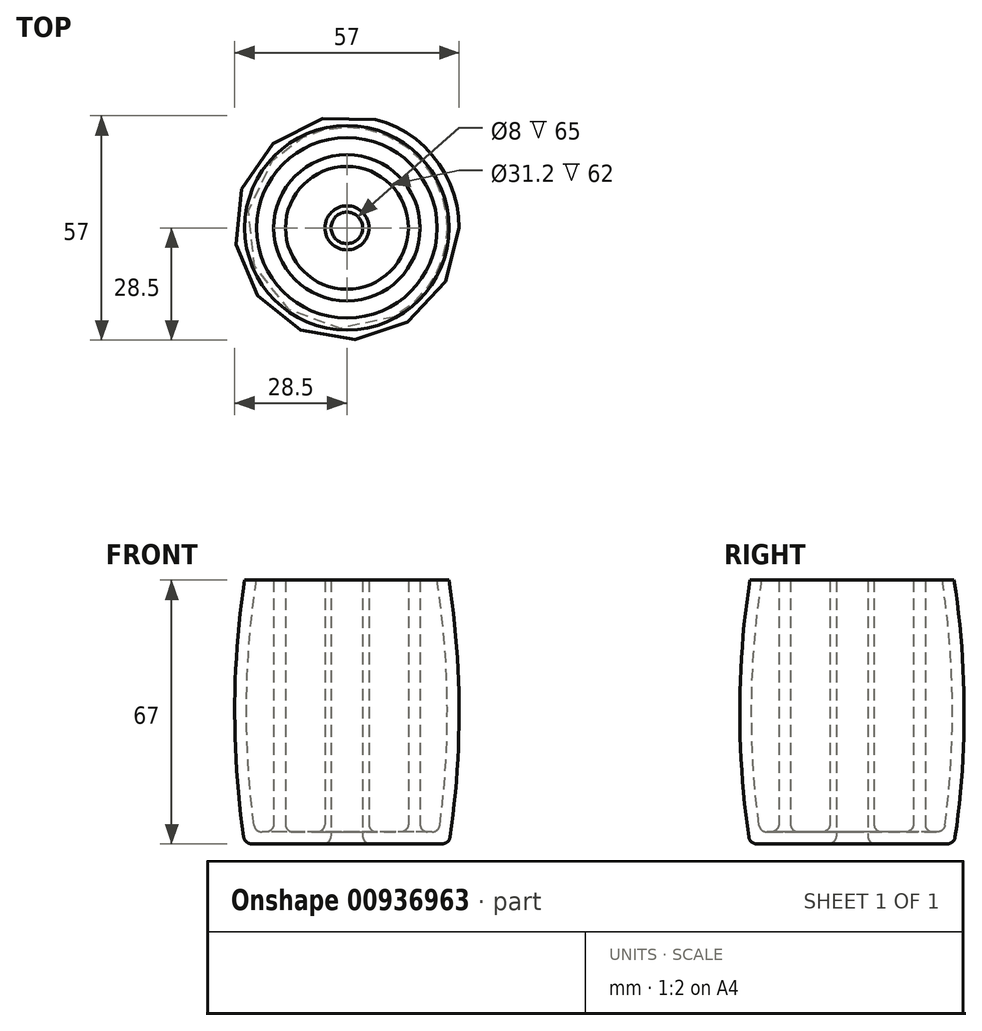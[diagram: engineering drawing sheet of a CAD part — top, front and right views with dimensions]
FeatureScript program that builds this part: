
annotation { "Feature Type Name" : "Feature", "Feature Type Description" : "" }
export const myFeature = defineFeature(function(context is Context, id is Id, definition is map)
    precondition{}
    {
        {
            var Q0;
            Q0=qCreatedBy(makeId("Front.planeOp"),FACE);
            var sketch = newSketch(context, id + "F0", { "sketchPlane" : qUnion([Q0])});
            skLineSegment(sketch, "E0", {"start": v(-4, 0) * mm, "end": v(-25.96, 0) * mm});
            skArc(sketch, "E1", {"start": v(-25.96, 67) * mm, "mid": v(-28.5, 33.5) * mm, "end": v(-25.96, 0) * mm});
            skLineSegment(sketch, "E2", {"start": v(-15.6, 67) * mm, "end": v(-15.6, 3) * mm});
            skLineSegment(sketch, "E3", {"start": v(-23.37, 3) * mm, "end": v(-18.6, 3) * mm});
            skLineSegment(sketch, "E4", {"start": v(-18.6, 3) * mm, "end": v(-18.6, 67) * mm});
            skArc(sketch, "E5", {"start": v(-22.92, 67) * mm, "mid": v(-25.5, 35.02) * mm, "end": v(-23.37, 3) * mm});
            skLineSegment(sketch, "E6", {"start": v(-5.6, 3) * mm, "end": v(-15.6, 3) * mm});
            skLineSegment(sketch, "E7", {"start": v(-15.6, 67) * mm, "end": v(-18.6, 67) * mm});
            skLineSegment(sketch, "E8", {"start": v(-4, 67) * mm, "end": v(-5.6, 67) * mm});
            skLineSegment(sketch, "E9", {"start": v(-22.92, 67) * mm, "end": v(-25.96, 67) * mm});
            skLineSegment(sketch, "E10", {"start": v(-4, 67) * mm, "end": v(-4, 0) * mm});
            skLineSegment(sketch, "E11", {"start": v(-5.6, 67) * mm, "end": v(-5.6, 3) * mm});
            skLineSegment(sketch, "E12", {"start": v(-5.6, 67) * mm, "end": v(-15.6, 67) * mm, "construction": true});
            skLineSegment(sketch, "E13", {"start": v(-18.6, 67) * mm, "end": v(-22.92, 67) * mm, "construction": true});
            skLineSegment(sketch, "E14", {"start": v(-25.96, 67) * mm, "end": v(-25.96, 0) * mm, "construction": true});
            skLineSegment(sketch, "E15", {"start": v(0, 0) * mm, "end": v(0, 67) * mm});
            skSolve(sketch);
        }
        {
            var Q0;
            Q0=makeQuery(id+"F0.imprint","IMPRINT",FACE,{"disambiguationData":[TD([[makeQuery(id+"F0.imprint","IMPRINT",EDGE,{"derivedFrom":sQuery(id+"F0.wireOp",EDGE,"E0")}),-1.0]])]});
            var Q1;
            Q1=sQuery(id+"F0.wireOp",EDGE,"E15");
            revolve(context, id + "F1", {"surfaceOperationType" : NewSurfaceOperationType.NEW, "entities" : qUnion([Q0]), "axis" : qUnion([Q1]), "revolveType" : RevolveType.FULL});
        }
        {
            var Q0;
            Q0=makeQuery(id+"F1.opRevolve","SWEPT_EDGE",EDGE,{"disambiguationData":[OSD([sQuery(id+"F0.wireOp",EDGE,"zfuqpYvi-nD6G-48Wu-hoye-4oUvRpUNeBjX"),sQuery(id+"F0.wireOp",EDGE,"YJsMTHjw-kJPD-WuPL-Lv33-pN4nG9kPYEEU")])]});
            var Q1;
            Q1=makeQuery(id+"F1.opRevolve","SWEPT_EDGE",EDGE,{"disambiguationData":[OSD([sQuery(id+"F0.wireOp",EDGE,"73oQLxVT-LSWg-F1Ge-i0z1-ve6tOWOdIWX1"),sQuery(id+"F0.wireOp",EDGE,"E6")])]});
            var Q2;
            Q2=makeQuery(id+"F1.opRevolve","SWEPT_EDGE",EDGE,{"disambiguationData":[OSD([sQuery(id+"F0.wireOp",EDGE,"E2"),sQuery(id+"F0.wireOp",EDGE,"E6")])]});
            var Q3;
            Q3=makeQuery(id+"F1.opRevolve","SWEPT_EDGE",EDGE,{"disambiguationData":[OSD([sQuery(id+"F0.wireOp",EDGE,"E3"),sQuery(id+"F0.wireOp",EDGE,"E5")])]});
            var Q4;
            Q4=makeQuery(id+"F1.opRevolve","SWEPT_EDGE",EDGE,{"disambiguationData":[OSD([sQuery(id+"F0.wireOp",EDGE,"E3"),sQuery(id+"F0.wireOp",EDGE,"E4")])]});
            var Q5;
            Q5=makeQuery(id+"F1.opRevolve","SWEPT_EDGE",EDGE,{"disambiguationData":[OSD([sQuery(id+"F0.wireOp",EDGE,"E0"),sQuery(id+"F0.wireOp",EDGE,"E10")])]});
            fillet(context, id + "F2", {"entities" : qUnion([Q0, Q1, Q2, Q3, Q4, Q5]), "radius" : 2 * mm, "tangentPropagation" : true, "allowEdgeOverflow" : false});
        }
        {
            var Q0;
            Q0=makeQuery(id+"F1.opRevolve","SWEPT_EDGE",EDGE,{"disambiguationData":[OSD([sQuery(id+"F0.wireOp",EDGE,"E0"),sQuery(id+"F0.wireOp",EDGE,"E1")])]});
            fillet(context, id + "F3", {"entities" : qUnion([Q0]), "radius" : 2 * mm, "tangentPropagation" : true, "allowEdgeOverflow" : false});
        }
    });
